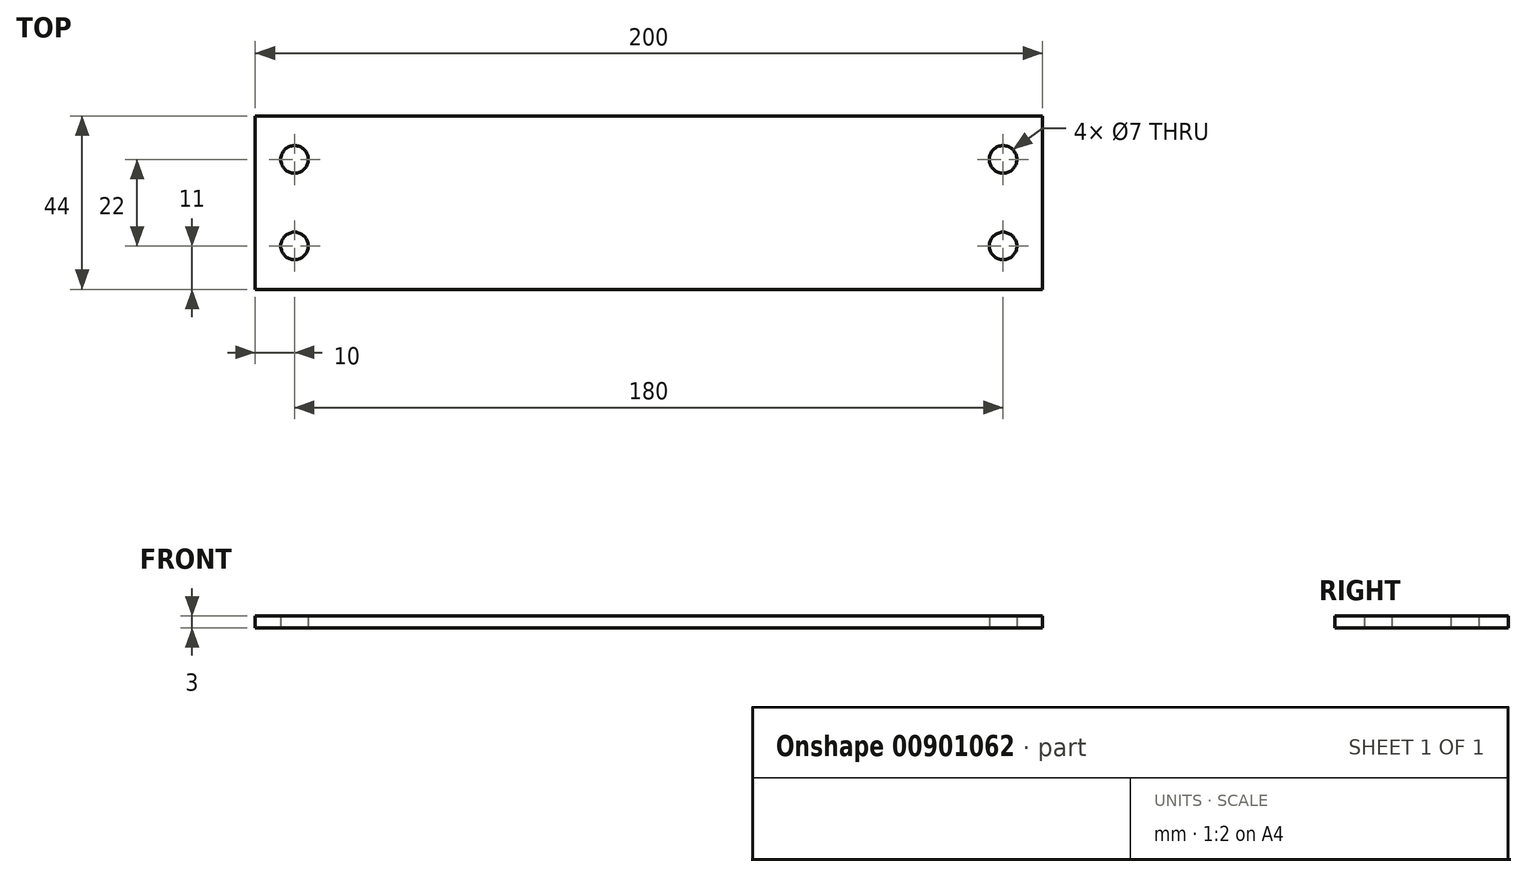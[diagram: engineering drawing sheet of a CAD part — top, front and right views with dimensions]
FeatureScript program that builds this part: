
annotation { "Feature Type Name" : "Feature", "Feature Type Description" : "" }
export const myFeature = defineFeature(function(context is Context, id is Id, definition is map)
    precondition{}
    {
        {
            var Q0;
            Q0=qCreatedBy(makeId("Top.planeOp"),FACE);
            var sketch = newSketch(context, id + "F0", { "sketchPlane" : qUnion([Q0])});
            skLineSegment(sketch, "E0.bottom", {"start": v(100, -22) * mm, "end": v(-100, -22) * mm});
            skLineSegment(sketch, "E0.top", {"start": v(100, 22) * mm, "end": v(-100, 22) * mm});
            skLineSegment(sketch, "E0.left", {"start": v(100, -22) * mm, "end": v(100, 22) * mm});
            skLineSegment(sketch, "E0.right", {"start": v(-100, -22) * mm, "end": v(-100, 22) * mm});
            skPoint(sketch, "E0.middle", {"position": v(0, 0) * mm});
            skCircle(sketch, "E1", {"center": v(-90, 11) * mm, "radius": 3.5 * mm});
            skCircle(sketch, "E2", {"center": v(-90, -11) * mm, "radius": 3.5 * mm});
            skCircle(sketch, "E3.MirrorC", {"center": v(90, 11) * mm, "radius": 3.5 * mm});
            skCircle(sketch, "E4.MirrorC", {"center": v(90, -11) * mm, "radius": 3.5 * mm});
            skSolve(sketch);
        }
        {
            var Q0;
            Q0=makeQuery(id+"F0.imprint","IMPRINT",FACE,{"disambiguationData":[TD([[makeQuery(id+"F0.imprint","IMPRINT",EDGE,{"derivedFrom":sQuery(id+"F0.wireOp",EDGE,"E0.bottom")}),-1.0]])]});
            extrude(context, id + "F1", {"entities" : qUnion([Q0]), "depth" : 3 * mm, "offsetDistance" : 25 * mm});
        }
    });
